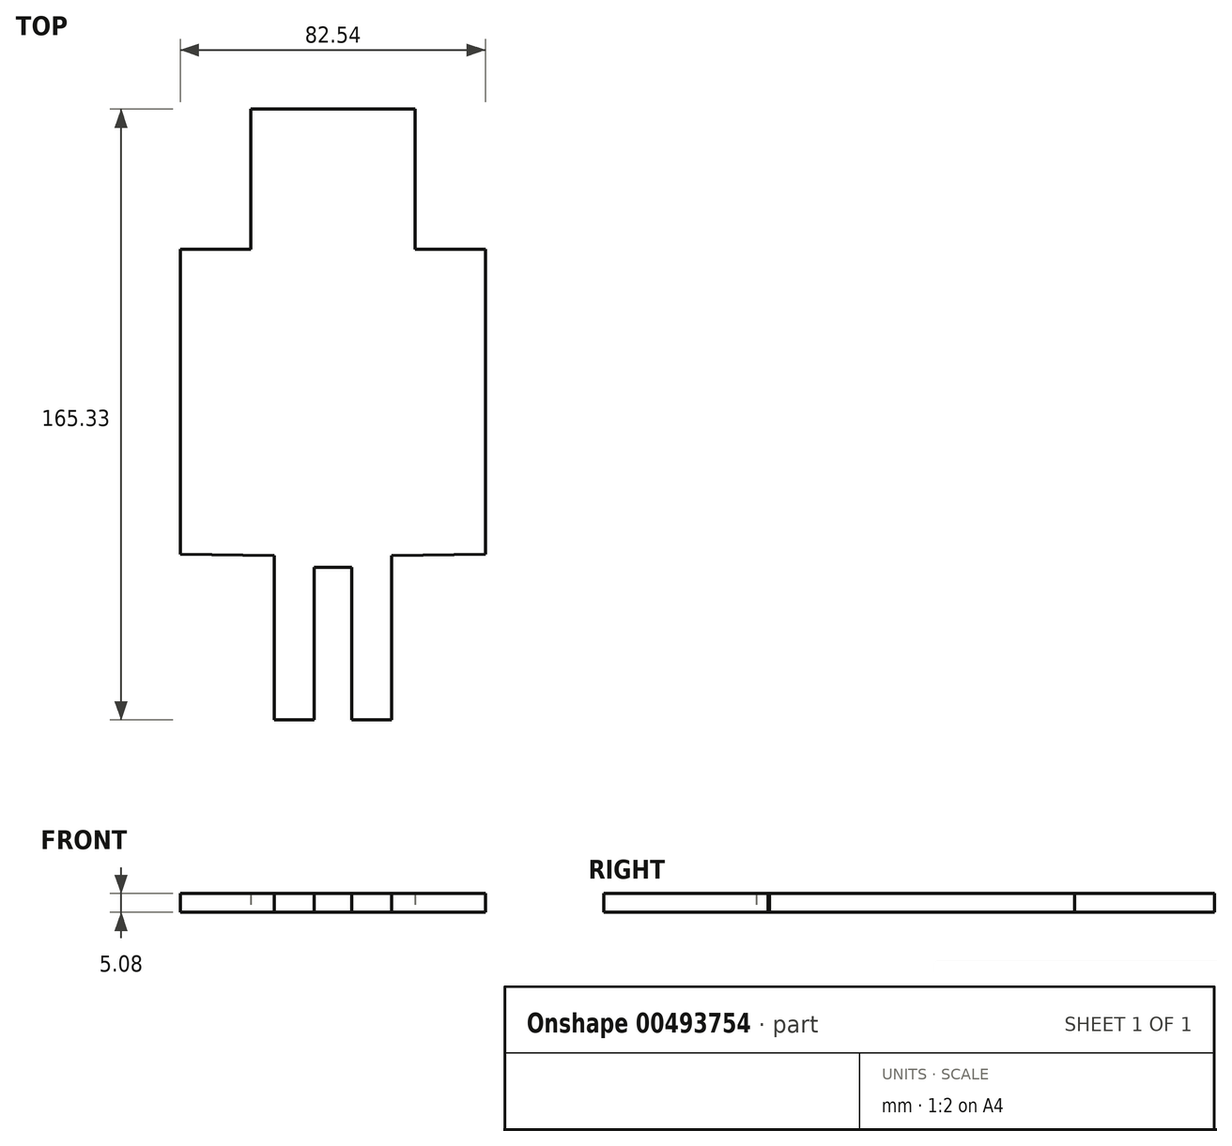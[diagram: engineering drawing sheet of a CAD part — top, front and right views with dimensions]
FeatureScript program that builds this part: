
annotation { "Feature Type Name" : "Feature", "Feature Type Description" : "" }
export const myFeature = defineFeature(function(context is Context, id is Id, definition is map)
    precondition{}
    {
        {
            var Q0;
            Q0=qCreatedBy(makeId("Top.planeOp"),FACE);
            var sketch = newSketch(context, id + "F0", { "sketchPlane" : qUnion([Q0])});
            skLineSegment(sketch, "E0.bottom", {"start": v(-21.66, 50.4) * mm, "end": v(22.78, 50.4) * mm});
            skLineSegment(sketch, "E0.left", {"start": v(-21.66, 50.4) * mm, "end": v(-21.66, 12.3) * mm});
            skLineSegment(sketch, "E0.right", {"start": v(22.78, 50.4) * mm, "end": v(22.78, 12.3) * mm});
            skLineSegment(sketch, "E1.bottom", {"start": v(-40.71, 12.5) * mm, "end": v(-21.66, 12.5) * mm});
            skLineSegment(sketch, "E1.left", {"start": v(-40.71, 12.5) * mm, "end": v(-40.71, -70.05) * mm});
            skLineSegment(sketch, "E1.right", {"start": v(41.83, 12.5) * mm, "end": v(41.83, -70.05) * mm});
            skLineSegment(sketch, "E2.top", {"start": v(-15.32, -114.92) * mm, "end": v(-4.52, -114.92) * mm});
            skLineSegment(sketch, "E2.left", {"start": v(-15.32, -70.47) * mm, "end": v(-15.32, -114.92) * mm});
            skLineSegment(sketch, "E2.right", {"start": v(16.43, -70.47) * mm, "end": v(16.43, -114.92) * mm});
            skLineSegment(sketch, "E3.trimOffspring", {"start": v(22.78, 12.5) * mm, "end": v(41.83, 12.5) * mm});
            skLineSegment(sketch, "E4", {"start": v(5.64, -73.64) * mm, "end": v(5.64, -114.92) * mm});
            skLineSegment(sketch, "E5", {"start": v(-4.52, -73.64) * mm, "end": v(-4.52, -114.92) * mm});
            skLineSegment(sketch, "E6", {"start": v(-4.52, -114.92) * mm, "end": v(-4.52, -73.64) * mm});
            skLineSegment(sketch, "E7", {"start": v(-4.52, -73.64) * mm, "end": v(5.64, -73.64) * mm});
            skLineSegment(sketch, "E8", {"start": v(5.64, -114.92) * mm, "end": v(16.43, -114.92) * mm});
            skLineSegment(sketch, "E9", {"start": v(-4.52, -114.92) * mm, "end": v(-15.32, -114.92) * mm});
            skLineSegment(sketch, "E10", {"start": v(16.43, -70.47) * mm, "end": v(41.83, -70.05) * mm});
            skLineSegment(sketch, "E11", {"start": v(-15.32, -70.47) * mm, "end": v(-40.71, -70.05) * mm});
            skSolve(sketch);
        }
        {
            var Q0;
            Q0 = qSketchRegion(id + "F0", true);
            extrude(context, id + "F1", {"entities" : qUnion([Q0]), "depth" : 5.08 * mm});
        }
    });
